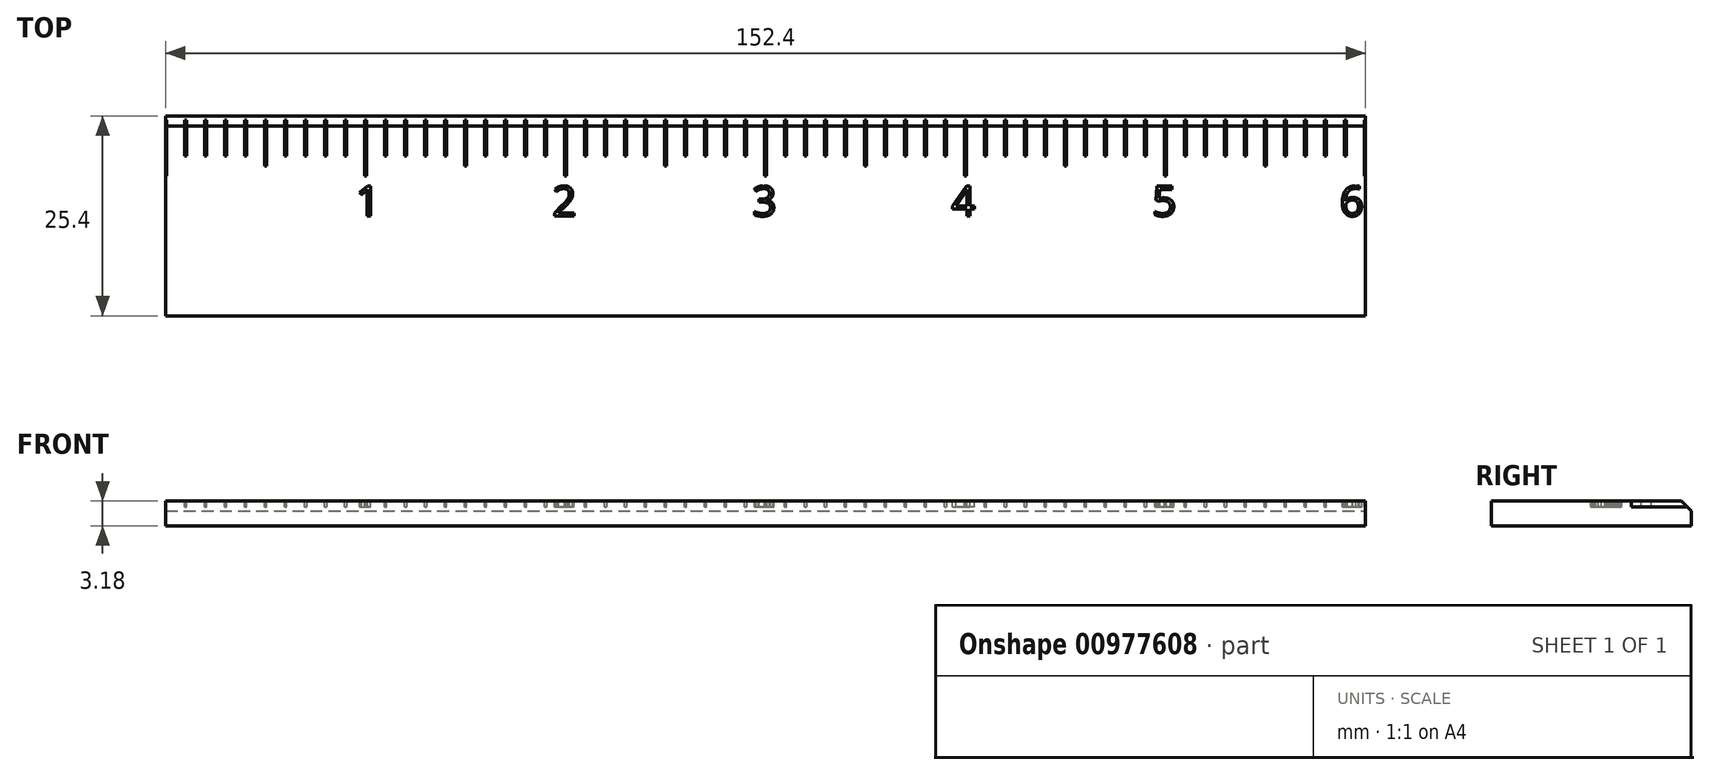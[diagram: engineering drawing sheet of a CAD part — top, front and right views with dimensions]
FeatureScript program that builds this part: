
annotation { "Feature Type Name" : "Feature", "Feature Type Description" : "" }
export const myFeature = defineFeature(function(context is Context, id is Id, definition is map)
    precondition{}
    {
        {
            var Q0;
            Q0=qCreatedBy(makeId("Top.planeOp"),FACE);
            var sketch = newSketch(context, id + "F0", { "sketchPlane" : qUnion([Q0])});
            skLineSegment(sketch, "E0.bottom", {"start": v(76.2, -12.7) * mm, "end": v(-76.2, -12.7) * mm});
            skLineSegment(sketch, "E0.top", {"start": v(76.2, 12.7) * mm, "end": v(-76.2, 12.7) * mm});
            skLineSegment(sketch, "E0.left", {"start": v(76.2, -12.7) * mm, "end": v(76.2, 12.7) * mm});
            skLineSegment(sketch, "E0.right", {"start": v(-76.2, -12.7) * mm, "end": v(-76.2, 12.7) * mm});
            skPoint(sketch, "E0.middle", {"position": v(0, 0) * mm});
            skSolve(sketch);
        }
        {
            var Q0;
            Q0 = qSketchRegion(id + "F0", true);
            extrude(context, id + "F1", {"entities" : qUnion([Q0]), "depth" : 3.17 * mm, "offsetDistance" : 25.4 * mm});
        }
        {
            var Q0;
            Q0=makeQuery(id+"F1.opExtrude","CAP_FACE",FACE,{"disambiguationData":[OSD([sQuery(id+"F0.wireOp",EDGE,"E0.bottom"),sQuery(id+"F0.wireOp",EDGE,"E0.top"),sQuery(id+"F0.wireOp",EDGE,"E0.left"),sQuery(id+"F0.wireOp",EDGE,"E0.right")])],"isStart":false});
            var sketch = newSketch(context, id + "F2", { "sketchPlane" : qUnion([Q0])});
            skLineSegment(sketch, "E1.bottom", {"start": v(-76.33, 12.7) * mm, "end": v(-76.07, 12.7) * mm});
            skLineSegment(sketch, "E1.top", {"start": v(-76.33, 5.08) * mm, "end": v(-76.07, 5.08) * mm});
            skLineSegment(sketch, "E1.left", {"start": v(-76.33, 12.7) * mm, "end": v(-76.33, 5.08) * mm});
            skLineSegment(sketch, "E1.right", {"start": v(-76.07, 12.7) * mm, "end": v(-76.07, 5.08) * mm});
            skLineSegment(sketch, "E2.bottom", {"start": v(-73.79, 12.7) * mm, "end": v(-73.53, 12.7) * mm});
            skLineSegment(sketch, "E2.top", {"start": v(-73.79, 7.62) * mm, "end": v(-73.53, 7.62) * mm});
            skLineSegment(sketch, "E2.left", {"start": v(-73.79, 12.7) * mm, "end": v(-73.79, 7.62) * mm});
            skLineSegment(sketch, "E2.right", {"start": v(-73.53, 12.7) * mm, "end": v(-73.53, 7.62) * mm});
            skLineSegment(sketch, "E3.1.0.0", {"start": v(-71.25, 12.7) * mm, "end": v(-71.25, 7.62) * mm});
            skLineSegment(sketch, "E3.1.0.1", {"start": v(-71, 12.7) * mm, "end": v(-71, 7.62) * mm});
            skLineSegment(sketch, "E3.1.0.2", {"start": v(-71.25, 12.7) * mm, "end": v(-71, 12.7) * mm});
            skLineSegment(sketch, "E3.1.0.3", {"start": v(-71.25, 7.62) * mm, "end": v(-71, 7.62) * mm});
            skLineSegment(sketch, "E3.2.0.0", {"start": v(-68.7, 12.7) * mm, "end": v(-68.7, 7.62) * mm});
            skLineSegment(sketch, "E3.2.0.1", {"start": v(-68.45, 12.7) * mm, "end": v(-68.45, 7.62) * mm});
            skLineSegment(sketch, "E3.2.0.2", {"start": v(-68.7, 12.7) * mm, "end": v(-68.45, 12.7) * mm});
            skLineSegment(sketch, "E3.2.0.3", {"start": v(-68.7, 7.62) * mm, "end": v(-68.45, 7.62) * mm});
            skLineSegment(sketch, "E3.3.0.0", {"start": v(-66.17, 12.7) * mm, "end": v(-66.17, 7.62) * mm});
            skLineSegment(sketch, "E3.3.0.1", {"start": v(-65.91, 12.7) * mm, "end": v(-65.91, 7.62) * mm});
            skLineSegment(sketch, "E3.3.0.2", {"start": v(-66.17, 12.7) * mm, "end": v(-65.91, 12.7) * mm});
            skLineSegment(sketch, "E3.3.0.3", {"start": v(-66.17, 7.62) * mm, "end": v(-65.91, 7.62) * mm});
            skLineSegment(sketch, "E3.direction1", {"start": v(-73.79, 7.62) * mm, "end": v(-71.25, 7.62) * mm, "construction": true});
            skLineSegment(sketch, "E4.bottom", {"start": v(-63.63, 12.7) * mm, "end": v(-63.37, 12.7) * mm});
            skLineSegment(sketch, "E4.top", {"start": v(-63.63, 6.35) * mm, "end": v(-63.37, 6.35) * mm});
            skLineSegment(sketch, "E4.left", {"start": v(-63.63, 12.7) * mm, "end": v(-63.63, 6.35) * mm});
            skLineSegment(sketch, "E4.right", {"start": v(-63.37, 12.7) * mm, "end": v(-63.37, 6.35) * mm});
            skLineSegment(sketch, "E5.bottom", {"start": v(-61.09, 12.7) * mm, "end": v(-60.83, 12.7) * mm});
            skLineSegment(sketch, "E5.top", {"start": v(-61.09, 7.62) * mm, "end": v(-60.83, 7.62) * mm});
            skLineSegment(sketch, "E5.left", {"start": v(-61.09, 12.7) * mm, "end": v(-61.09, 7.62) * mm});
            skLineSegment(sketch, "E5.right", {"start": v(-60.83, 12.7) * mm, "end": v(-60.83, 7.62) * mm});
            skLineSegment(sketch, "E6.1.0.0", {"start": v(-58.3, 12.7) * mm, "end": v(-58.3, 7.62) * mm});
            skLineSegment(sketch, "E6.1.0.1", {"start": v(-58.55, 12.7) * mm, "end": v(-58.55, 7.62) * mm});
            skLineSegment(sketch, "E6.1.0.2", {"start": v(-58.55, 12.7) * mm, "end": v(-58.3, 12.7) * mm});
            skLineSegment(sketch, "E6.1.0.3", {"start": v(-58.55, 7.62) * mm, "end": v(-58.3, 7.62) * mm});
            skLineSegment(sketch, "E6.2.0.0", {"start": v(-55.75, 12.7) * mm, "end": v(-55.75, 7.62) * mm});
            skLineSegment(sketch, "E6.2.0.1", {"start": v(-56, 12.7) * mm, "end": v(-56, 7.62) * mm});
            skLineSegment(sketch, "E6.2.0.2", {"start": v(-56, 12.7) * mm, "end": v(-55.75, 12.7) * mm});
            skLineSegment(sketch, "E6.2.0.3", {"start": v(-56, 7.62) * mm, "end": v(-55.75, 7.62) * mm});
            skLineSegment(sketch, "E6.3.0.0", {"start": v(-53.21, 12.7) * mm, "end": v(-53.21, 7.62) * mm});
            skLineSegment(sketch, "E6.3.0.1", {"start": v(-53.47, 12.7) * mm, "end": v(-53.47, 7.62) * mm});
            skLineSegment(sketch, "E6.3.0.2", {"start": v(-53.47, 12.7) * mm, "end": v(-53.21, 12.7) * mm});
            skLineSegment(sketch, "E6.3.0.3", {"start": v(-53.47, 7.62) * mm, "end": v(-53.21, 7.62) * mm});
            skLineSegment(sketch, "E6.direction1", {"start": v(-61.09, 7.62) * mm, "end": v(-58.55, 7.62) * mm, "construction": true});
            skLineSegment(sketch, "E7.bottom", {"start": v(-50.93, 12.7) * mm, "end": v(-50.67, 12.7) * mm});
            skLineSegment(sketch, "E7.top", {"start": v(-50.93, 5.08) * mm, "end": v(-50.67, 5.08) * mm});
            skLineSegment(sketch, "E7.left", {"start": v(-50.93, 12.7) * mm, "end": v(-50.93, 5.08) * mm});
            skLineSegment(sketch, "E7.right", {"start": v(-50.67, 12.7) * mm, "end": v(-50.67, 5.08) * mm});
            skLineSegment(sketch, "E8.1.0.0", {"start": v(-45.6, 12.7) * mm, "end": v(-45.6, 7.62) * mm});
            skLineSegment(sketch, "E8.1.0.2", {"start": v(-48.39, 12.7) * mm, "end": v(-48.39, 7.62) * mm});
            skLineSegment(sketch, "E8.1.0.3", {"start": v(-33.15, 12.7) * mm, "end": v(-33.15, 7.62) * mm});
            skLineSegment(sketch, "E8.1.0.4", {"start": v(-32.9, 12.7) * mm, "end": v(-32.9, 7.62) * mm});
            skLineSegment(sketch, "E8.1.0.5", {"start": v(-45.85, 12.7) * mm, "end": v(-45.85, 7.62) * mm});
            skLineSegment(sketch, "E8.1.0.6", {"start": v(-35.69, 12.7) * mm, "end": v(-35.69, 7.62) * mm});
            skLineSegment(sketch, "E8.1.0.7", {"start": v(-30.6, 12.7) * mm, "end": v(-30.6, 7.62) * mm});
            skLineSegment(sketch, "E8.1.0.8", {"start": v(-38.23, 12.7) * mm, "end": v(-38.23, 6.35) * mm});
            skLineSegment(sketch, "E8.1.0.9", {"start": v(-43.05, 12.7) * mm, "end": v(-43.05, 7.62) * mm});
            skLineSegment(sketch, "E8.1.0.10", {"start": v(-35.43, 12.7) * mm, "end": v(-35.43, 7.62) * mm});
            skLineSegment(sketch, "E8.1.0.11", {"start": v(-48.13, 12.7) * mm, "end": v(-48.13, 7.62) * mm});
            skLineSegment(sketch, "E8.1.0.12", {"start": v(-40.77, 12.7) * mm, "end": v(-40.77, 7.62) * mm});
            skLineSegment(sketch, "E8.1.0.13", {"start": v(-25.53, 12.7) * mm, "end": v(-25.53, 5.08) * mm});
            skLineSegment(sketch, "E8.1.0.14", {"start": v(-37.97, 12.7) * mm, "end": v(-37.97, 6.35) * mm});
            skLineSegment(sketch, "E8.1.0.15", {"start": v(-43.3, 12.7) * mm, "end": v(-43.3, 7.62) * mm});
            skLineSegment(sketch, "E8.1.0.17", {"start": v(-27.81, 12.7) * mm, "end": v(-27.81, 7.62) * mm});
            skLineSegment(sketch, "E8.1.0.18", {"start": v(-48.39, 7.62) * mm, "end": v(-45.85, 7.62) * mm, "construction": true});
            skLineSegment(sketch, "E8.1.0.19", {"start": v(-30.35, 12.7) * mm, "end": v(-30.35, 7.62) * mm});
            skLineSegment(sketch, "E8.1.0.20", {"start": v(-25.27, 12.7) * mm, "end": v(-25.27, 5.08) * mm});
            skLineSegment(sketch, "E8.1.0.21", {"start": v(-35.69, 7.62) * mm, "end": v(-33.15, 7.62) * mm, "construction": true});
            skLineSegment(sketch, "E8.1.0.22", {"start": v(-40.51, 12.7) * mm, "end": v(-40.51, 7.62) * mm});
            skLineSegment(sketch, "E8.1.0.23", {"start": v(-28.07, 12.7) * mm, "end": v(-28.07, 7.62) * mm});
            skLineSegment(sketch, "E8.1.0.24", {"start": v(-30.6, 7.62) * mm, "end": v(-30.35, 7.62) * mm});
            skLineSegment(sketch, "E8.1.0.25", {"start": v(-40.77, 12.7) * mm, "end": v(-40.51, 12.7) * mm});
            skLineSegment(sketch, "E8.1.0.26", {"start": v(-45.85, 12.7) * mm, "end": v(-45.6, 12.7) * mm});
            skLineSegment(sketch, "E8.1.0.27", {"start": v(-40.77, 7.62) * mm, "end": v(-40.51, 7.62) * mm});
            skLineSegment(sketch, "E8.1.0.28", {"start": v(-33.15, 12.7) * mm, "end": v(-32.9, 12.7) * mm});
            skLineSegment(sketch, "E8.1.0.29", {"start": v(-30.6, 12.7) * mm, "end": v(-30.35, 12.7) * mm});
            skLineSegment(sketch, "E8.1.0.30", {"start": v(-38.23, 12.7) * mm, "end": v(-37.97, 12.7) * mm});
            skLineSegment(sketch, "E8.1.0.33", {"start": v(-35.69, 12.7) * mm, "end": v(-35.43, 12.7) * mm});
            skLineSegment(sketch, "E8.1.0.34", {"start": v(-48.39, 12.7) * mm, "end": v(-48.13, 12.7) * mm});
            skLineSegment(sketch, "E8.1.0.35", {"start": v(-25.53, 5.08) * mm, "end": v(-25.27, 5.08) * mm});
            skLineSegment(sketch, "E8.1.0.36", {"start": v(-25.53, 12.7) * mm, "end": v(-25.27, 12.7) * mm});
            skLineSegment(sketch, "E8.1.0.37", {"start": v(-43.3, 12.7) * mm, "end": v(-43.05, 12.7) * mm});
            skLineSegment(sketch, "E8.1.0.38", {"start": v(-38.23, 6.35) * mm, "end": v(-37.97, 6.35) * mm});
            skLineSegment(sketch, "E8.1.0.39", {"start": v(-43.3, 7.62) * mm, "end": v(-43.05, 7.62) * mm});
            skLineSegment(sketch, "E8.1.0.40", {"start": v(-48.39, 7.62) * mm, "end": v(-48.13, 7.62) * mm});
            skLineSegment(sketch, "E8.1.0.41", {"start": v(-33.15, 7.62) * mm, "end": v(-32.9, 7.62) * mm});
            skLineSegment(sketch, "E8.1.0.42", {"start": v(-35.69, 7.62) * mm, "end": v(-35.43, 7.62) * mm});
            skLineSegment(sketch, "E8.1.0.43", {"start": v(-45.85, 7.62) * mm, "end": v(-45.6, 7.62) * mm});
            skLineSegment(sketch, "E8.1.0.44", {"start": v(-28.07, 7.62) * mm, "end": v(-27.81, 7.62) * mm});
            skLineSegment(sketch, "E8.1.0.45", {"start": v(-28.07, 12.7) * mm, "end": v(-27.81, 12.7) * mm});
            skLineSegment(sketch, "E8.2.0.0", {"start": v(-20.2, 12.7) * mm, "end": v(-20.2, 7.62) * mm});
            skLineSegment(sketch, "E8.2.0.1", {"start": v(-25.27, 12.7) * mm, "end": v(-25.27, 5.08) * mm});
            skLineSegment(sketch, "E8.2.0.2", {"start": v(-22.99, 12.7) * mm, "end": v(-22.99, 7.62) * mm});
            skLineSegment(sketch, "E8.2.0.3", {"start": v(-7.75, 12.7) * mm, "end": v(-7.75, 7.62) * mm});
            skLineSegment(sketch, "E8.2.0.4", {"start": v(-7.5, 12.7) * mm, "end": v(-7.5, 7.62) * mm});
            skLineSegment(sketch, "E8.2.0.5", {"start": v(-20.45, 12.7) * mm, "end": v(-20.45, 7.62) * mm});
            skLineSegment(sketch, "E8.2.0.6", {"start": v(-10.29, 12.7) * mm, "end": v(-10.29, 7.62) * mm});
            skLineSegment(sketch, "E8.2.0.7", {"start": v(-5.2, 12.7) * mm, "end": v(-5.2, 7.62) * mm});
            skLineSegment(sketch, "E8.2.0.8", {"start": v(-12.83, 12.7) * mm, "end": v(-12.83, 6.35) * mm});
            skLineSegment(sketch, "E8.2.0.9", {"start": v(-17.65, 12.7) * mm, "end": v(-17.65, 7.62) * mm});
            skLineSegment(sketch, "E8.2.0.10", {"start": v(-10.03, 12.7) * mm, "end": v(-10.03, 7.62) * mm});
            skLineSegment(sketch, "E8.2.0.11", {"start": v(-22.73, 12.7) * mm, "end": v(-22.73, 7.62) * mm});
            skLineSegment(sketch, "E8.2.0.12", {"start": v(-15.37, 12.7) * mm, "end": v(-15.37, 7.62) * mm});
            skLineSegment(sketch, "E8.2.0.13", {"start": v(-0.13, 12.7) * mm, "end": v(-0.13, 5.08) * mm});
            skLineSegment(sketch, "E8.2.0.14", {"start": v(-12.57, 12.7) * mm, "end": v(-12.57, 6.35) * mm});
            skLineSegment(sketch, "E8.2.0.15", {"start": v(-17.9, 12.7) * mm, "end": v(-17.9, 7.62) * mm});
            skLineSegment(sketch, "E8.2.0.16", {"start": v(-25.53, 12.7) * mm, "end": v(-25.53, 5.08) * mm});
            skLineSegment(sketch, "E8.2.0.17", {"start": v(-2.41, 12.7) * mm, "end": v(-2.41, 7.62) * mm});
            skLineSegment(sketch, "E8.2.0.18", {"start": v(-22.99, 7.62) * mm, "end": v(-20.45, 7.62) * mm, "construction": true});
            skLineSegment(sketch, "E8.2.0.19", {"start": v(-4.95, 12.7) * mm, "end": v(-4.95, 7.62) * mm});
            skLineSegment(sketch, "E8.2.0.20", {"start": v(0.13, 12.7) * mm, "end": v(0.13, 5.08) * mm});
            skLineSegment(sketch, "E8.2.0.21", {"start": v(-10.29, 7.62) * mm, "end": v(-7.75, 7.62) * mm, "construction": true});
            skLineSegment(sketch, "E8.2.0.22", {"start": v(-15.11, 12.7) * mm, "end": v(-15.11, 7.62) * mm});
            skLineSegment(sketch, "E8.2.0.23", {"start": v(-2.67, 12.7) * mm, "end": v(-2.67, 7.62) * mm});
            skLineSegment(sketch, "E8.2.0.24", {"start": v(-5.2, 7.62) * mm, "end": v(-4.95, 7.62) * mm});
            skLineSegment(sketch, "E8.2.0.25", {"start": v(-15.37, 12.7) * mm, "end": v(-15.11, 12.7) * mm});
            skLineSegment(sketch, "E8.2.0.26", {"start": v(-20.45, 12.7) * mm, "end": v(-20.2, 12.7) * mm});
            skLineSegment(sketch, "E8.2.0.27", {"start": v(-15.37, 7.62) * mm, "end": v(-15.11, 7.62) * mm});
            skLineSegment(sketch, "E8.2.0.28", {"start": v(-7.75, 12.7) * mm, "end": v(-7.5, 12.7) * mm});
            skLineSegment(sketch, "E8.2.0.29", {"start": v(-5.2, 12.7) * mm, "end": v(-4.95, 12.7) * mm});
            skLineSegment(sketch, "E8.2.0.30", {"start": v(-12.83, 12.7) * mm, "end": v(-12.57, 12.7) * mm});
            skLineSegment(sketch, "E8.2.0.31", {"start": v(-25.53, 5.08) * mm, "end": v(-25.27, 5.08) * mm});
            skLineSegment(sketch, "E8.2.0.32", {"start": v(-25.53, 12.7) * mm, "end": v(-25.27, 12.7) * mm});
            skLineSegment(sketch, "E8.2.0.33", {"start": v(-10.29, 12.7) * mm, "end": v(-10.03, 12.7) * mm});
            skLineSegment(sketch, "E8.2.0.34", {"start": v(-22.99, 12.7) * mm, "end": v(-22.73, 12.7) * mm});
            skLineSegment(sketch, "E8.2.0.35", {"start": v(-0.13, 5.08) * mm, "end": v(0.13, 5.08) * mm});
            skLineSegment(sketch, "E8.2.0.36", {"start": v(-0.13, 12.7) * mm, "end": v(0.13, 12.7) * mm});
            skLineSegment(sketch, "E8.2.0.37", {"start": v(-17.9, 12.7) * mm, "end": v(-17.65, 12.7) * mm});
            skLineSegment(sketch, "E8.2.0.38", {"start": v(-12.83, 6.35) * mm, "end": v(-12.57, 6.35) * mm});
            skLineSegment(sketch, "E8.2.0.39", {"start": v(-17.9, 7.62) * mm, "end": v(-17.65, 7.62) * mm});
            skLineSegment(sketch, "E8.2.0.40", {"start": v(-22.99, 7.62) * mm, "end": v(-22.73, 7.62) * mm});
            skLineSegment(sketch, "E8.2.0.41", {"start": v(-7.75, 7.62) * mm, "end": v(-7.5, 7.62) * mm});
            skLineSegment(sketch, "E8.2.0.42", {"start": v(-10.29, 7.62) * mm, "end": v(-10.03, 7.62) * mm});
            skLineSegment(sketch, "E8.2.0.43", {"start": v(-20.45, 7.62) * mm, "end": v(-20.2, 7.62) * mm});
            skLineSegment(sketch, "E8.2.0.44", {"start": v(-2.67, 7.62) * mm, "end": v(-2.41, 7.62) * mm});
            skLineSegment(sketch, "E8.2.0.45", {"start": v(-2.67, 12.7) * mm, "end": v(-2.41, 12.7) * mm});
            skLineSegment(sketch, "E8.3.0.0", {"start": v(5.2, 12.7) * mm, "end": v(5.2, 7.62) * mm});
            skLineSegment(sketch, "E8.3.0.1", {"start": v(0.13, 12.7) * mm, "end": v(0.13, 5.08) * mm});
            skLineSegment(sketch, "E8.3.0.2", {"start": v(2.41, 12.7) * mm, "end": v(2.41, 7.62) * mm});
            skLineSegment(sketch, "E8.3.0.3", {"start": v(17.65, 12.7) * mm, "end": v(17.65, 7.62) * mm});
            skLineSegment(sketch, "E8.3.0.4", {"start": v(17.9, 12.7) * mm, "end": v(17.9, 7.62) * mm});
            skLineSegment(sketch, "E8.3.0.5", {"start": v(4.95, 12.7) * mm, "end": v(4.95, 7.62) * mm});
            skLineSegment(sketch, "E8.3.0.6", {"start": v(15.11, 12.7) * mm, "end": v(15.11, 7.62) * mm});
            skLineSegment(sketch, "E8.3.0.7", {"start": v(20.2, 12.7) * mm, "end": v(20.2, 7.62) * mm});
            skLineSegment(sketch, "E8.3.0.8", {"start": v(12.57, 12.7) * mm, "end": v(12.57, 6.35) * mm});
            skLineSegment(sketch, "E8.3.0.9", {"start": v(7.75, 12.7) * mm, "end": v(7.75, 7.62) * mm});
            skLineSegment(sketch, "E8.3.0.10", {"start": v(15.37, 12.7) * mm, "end": v(15.37, 7.62) * mm});
            skLineSegment(sketch, "E8.3.0.11", {"start": v(2.67, 12.7) * mm, "end": v(2.67, 7.62) * mm});
            skLineSegment(sketch, "E8.3.0.12", {"start": v(10.03, 12.7) * mm, "end": v(10.03, 7.62) * mm});
            skLineSegment(sketch, "E8.3.0.13", {"start": v(25.27, 12.7) * mm, "end": v(25.27, 5.08) * mm});
            skLineSegment(sketch, "E8.3.0.14", {"start": v(12.83, 12.7) * mm, "end": v(12.83, 6.35) * mm});
            skLineSegment(sketch, "E8.3.0.15", {"start": v(7.5, 12.7) * mm, "end": v(7.5, 7.62) * mm});
            skLineSegment(sketch, "E8.3.0.16", {"start": v(-0.13, 12.7) * mm, "end": v(-0.13, 5.08) * mm});
            skLineSegment(sketch, "E8.3.0.17", {"start": v(22.99, 12.7) * mm, "end": v(22.99, 7.62) * mm});
            skLineSegment(sketch, "E8.3.0.18", {"start": v(2.41, 7.62) * mm, "end": v(4.95, 7.62) * mm, "construction": true});
            skLineSegment(sketch, "E8.3.0.19", {"start": v(20.45, 12.7) * mm, "end": v(20.45, 7.62) * mm});
            skLineSegment(sketch, "E8.3.0.20", {"start": v(25.53, 12.7) * mm, "end": v(25.53, 5.08) * mm});
            skLineSegment(sketch, "E8.3.0.21", {"start": v(15.11, 7.62) * mm, "end": v(17.65, 7.62) * mm, "construction": true});
            skLineSegment(sketch, "E8.3.0.22", {"start": v(10.29, 12.7) * mm, "end": v(10.29, 7.62) * mm});
            skLineSegment(sketch, "E8.3.0.23", {"start": v(22.73, 12.7) * mm, "end": v(22.73, 7.62) * mm});
            skLineSegment(sketch, "E8.3.0.24", {"start": v(20.2, 7.62) * mm, "end": v(20.45, 7.62) * mm});
            skLineSegment(sketch, "E8.3.0.25", {"start": v(10.03, 12.7) * mm, "end": v(10.29, 12.7) * mm});
            skLineSegment(sketch, "E8.3.0.26", {"start": v(4.95, 12.7) * mm, "end": v(5.2, 12.7) * mm});
            skLineSegment(sketch, "E8.3.0.27", {"start": v(10.03, 7.62) * mm, "end": v(10.29, 7.62) * mm});
            skLineSegment(sketch, "E8.3.0.28", {"start": v(17.65, 12.7) * mm, "end": v(17.9, 12.7) * mm});
            skLineSegment(sketch, "E8.3.0.29", {"start": v(20.2, 12.7) * mm, "end": v(20.45, 12.7) * mm});
            skLineSegment(sketch, "E8.3.0.30", {"start": v(12.57, 12.7) * mm, "end": v(12.83, 12.7) * mm});
            skLineSegment(sketch, "E8.3.0.31", {"start": v(-0.13, 5.08) * mm, "end": v(0.13, 5.08) * mm});
            skLineSegment(sketch, "E8.3.0.32", {"start": v(-0.13, 12.7) * mm, "end": v(0.13, 12.7) * mm});
            skLineSegment(sketch, "E8.3.0.33", {"start": v(15.11, 12.7) * mm, "end": v(15.37, 12.7) * mm});
            skLineSegment(sketch, "E8.3.0.34", {"start": v(2.41, 12.7) * mm, "end": v(2.67, 12.7) * mm});
            skLineSegment(sketch, "E8.3.0.35", {"start": v(25.27, 5.08) * mm, "end": v(25.53, 5.08) * mm});
            skLineSegment(sketch, "E8.3.0.36", {"start": v(25.27, 12.7) * mm, "end": v(25.53, 12.7) * mm});
            skLineSegment(sketch, "E8.3.0.37", {"start": v(7.5, 12.7) * mm, "end": v(7.75, 12.7) * mm});
            skLineSegment(sketch, "E8.3.0.38", {"start": v(12.57, 6.35) * mm, "end": v(12.83, 6.35) * mm});
            skLineSegment(sketch, "E8.3.0.39", {"start": v(7.5, 7.62) * mm, "end": v(7.75, 7.62) * mm});
            skLineSegment(sketch, "E8.3.0.40", {"start": v(2.41, 7.62) * mm, "end": v(2.67, 7.62) * mm});
            skLineSegment(sketch, "E8.3.0.41", {"start": v(17.65, 7.62) * mm, "end": v(17.9, 7.62) * mm});
            skLineSegment(sketch, "E8.3.0.42", {"start": v(15.11, 7.62) * mm, "end": v(15.37, 7.62) * mm});
            skLineSegment(sketch, "E8.3.0.43", {"start": v(4.95, 7.62) * mm, "end": v(5.2, 7.62) * mm});
            skLineSegment(sketch, "E8.3.0.44", {"start": v(22.73, 7.62) * mm, "end": v(22.99, 7.62) * mm});
            skLineSegment(sketch, "E8.3.0.45", {"start": v(22.73, 12.7) * mm, "end": v(22.99, 12.7) * mm});
            skLineSegment(sketch, "E8.4.0.0", {"start": v(30.6, 12.7) * mm, "end": v(30.6, 7.62) * mm});
            skLineSegment(sketch, "E8.4.0.1", {"start": v(25.53, 12.7) * mm, "end": v(25.53, 5.08) * mm});
            skLineSegment(sketch, "E8.4.0.2", {"start": v(27.81, 12.7) * mm, "end": v(27.81, 7.62) * mm});
            skLineSegment(sketch, "E8.4.0.3", {"start": v(43.05, 12.7) * mm, "end": v(43.05, 7.62) * mm});
            skLineSegment(sketch, "E8.4.0.4", {"start": v(43.3, 12.7) * mm, "end": v(43.3, 7.62) * mm});
            skLineSegment(sketch, "E8.4.0.5", {"start": v(30.35, 12.7) * mm, "end": v(30.35, 7.62) * mm});
            skLineSegment(sketch, "E8.4.0.6", {"start": v(40.51, 12.7) * mm, "end": v(40.51, 7.62) * mm});
            skLineSegment(sketch, "E8.4.0.7", {"start": v(45.6, 12.7) * mm, "end": v(45.6, 7.62) * mm});
            skLineSegment(sketch, "E8.4.0.8", {"start": v(37.97, 12.7) * mm, "end": v(37.97, 6.35) * mm});
            skLineSegment(sketch, "E8.4.0.9", {"start": v(33.15, 12.7) * mm, "end": v(33.15, 7.62) * mm});
            skLineSegment(sketch, "E8.4.0.10", {"start": v(40.77, 12.7) * mm, "end": v(40.77, 7.62) * mm});
            skLineSegment(sketch, "E8.4.0.11", {"start": v(28.07, 12.7) * mm, "end": v(28.07, 7.62) * mm});
            skLineSegment(sketch, "E8.4.0.12", {"start": v(35.43, 12.7) * mm, "end": v(35.43, 7.62) * mm});
            skLineSegment(sketch, "E8.4.0.13", {"start": v(50.67, 12.7) * mm, "end": v(50.67, 5.08) * mm});
            skLineSegment(sketch, "E8.4.0.14", {"start": v(38.23, 12.7) * mm, "end": v(38.23, 6.35) * mm});
            skLineSegment(sketch, "E8.4.0.15", {"start": v(32.9, 12.7) * mm, "end": v(32.9, 7.62) * mm});
            skLineSegment(sketch, "E8.4.0.16", {"start": v(25.27, 12.7) * mm, "end": v(25.27, 5.08) * mm});
            skLineSegment(sketch, "E8.4.0.17", {"start": v(48.39, 12.7) * mm, "end": v(48.39, 7.62) * mm});
            skLineSegment(sketch, "E8.4.0.18", {"start": v(27.81, 7.62) * mm, "end": v(30.35, 7.62) * mm, "construction": true});
            skLineSegment(sketch, "E8.4.0.19", {"start": v(45.85, 12.7) * mm, "end": v(45.85, 7.62) * mm});
            skLineSegment(sketch, "E8.4.0.20", {"start": v(50.93, 12.7) * mm, "end": v(50.93, 5.08) * mm});
            skLineSegment(sketch, "E8.4.0.21", {"start": v(40.51, 7.62) * mm, "end": v(43.05, 7.62) * mm, "construction": true});
            skLineSegment(sketch, "E8.4.0.22", {"start": v(35.69, 12.7) * mm, "end": v(35.69, 7.62) * mm});
            skLineSegment(sketch, "E8.4.0.23", {"start": v(48.13, 12.7) * mm, "end": v(48.13, 7.62) * mm});
            skLineSegment(sketch, "E8.4.0.24", {"start": v(45.6, 7.62) * mm, "end": v(45.85, 7.62) * mm});
            skLineSegment(sketch, "E8.4.0.25", {"start": v(35.43, 12.7) * mm, "end": v(35.69, 12.7) * mm});
            skLineSegment(sketch, "E8.4.0.26", {"start": v(30.35, 12.7) * mm, "end": v(30.6, 12.7) * mm});
            skLineSegment(sketch, "E8.4.0.27", {"start": v(35.43, 7.62) * mm, "end": v(35.69, 7.62) * mm});
            skLineSegment(sketch, "E8.4.0.28", {"start": v(43.05, 12.7) * mm, "end": v(43.3, 12.7) * mm});
            skLineSegment(sketch, "E8.4.0.29", {"start": v(45.6, 12.7) * mm, "end": v(45.85, 12.7) * mm});
            skLineSegment(sketch, "E8.4.0.30", {"start": v(37.97, 12.7) * mm, "end": v(38.23, 12.7) * mm});
            skLineSegment(sketch, "E8.4.0.31", {"start": v(25.27, 5.08) * mm, "end": v(25.53, 5.08) * mm});
            skLineSegment(sketch, "E8.4.0.32", {"start": v(25.27, 12.7) * mm, "end": v(25.53, 12.7) * mm});
            skLineSegment(sketch, "E8.4.0.33", {"start": v(40.51, 12.7) * mm, "end": v(40.77, 12.7) * mm});
            skLineSegment(sketch, "E8.4.0.34", {"start": v(27.81, 12.7) * mm, "end": v(28.07, 12.7) * mm});
            skLineSegment(sketch, "E8.4.0.35", {"start": v(50.67, 5.08) * mm, "end": v(50.93, 5.08) * mm});
            skLineSegment(sketch, "E8.4.0.36", {"start": v(50.67, 12.7) * mm, "end": v(50.93, 12.7) * mm});
            skLineSegment(sketch, "E8.4.0.37", {"start": v(32.9, 12.7) * mm, "end": v(33.15, 12.7) * mm});
            skLineSegment(sketch, "E8.4.0.38", {"start": v(37.97, 6.35) * mm, "end": v(38.23, 6.35) * mm});
            skLineSegment(sketch, "E8.4.0.39", {"start": v(32.9, 7.62) * mm, "end": v(33.15, 7.62) * mm});
            skLineSegment(sketch, "E8.4.0.40", {"start": v(27.81, 7.62) * mm, "end": v(28.07, 7.62) * mm});
            skLineSegment(sketch, "E8.4.0.41", {"start": v(43.05, 7.62) * mm, "end": v(43.3, 7.62) * mm});
            skLineSegment(sketch, "E8.4.0.42", {"start": v(40.51, 7.62) * mm, "end": v(40.77, 7.62) * mm});
            skLineSegment(sketch, "E8.4.0.43", {"start": v(30.35, 7.62) * mm, "end": v(30.6, 7.62) * mm});
            skLineSegment(sketch, "E8.4.0.44", {"start": v(48.13, 7.62) * mm, "end": v(48.39, 7.62) * mm});
            skLineSegment(sketch, "E8.4.0.45", {"start": v(48.13, 12.7) * mm, "end": v(48.39, 12.7) * mm});
            skLineSegment(sketch, "E8.5.0.0", {"start": v(56, 12.7) * mm, "end": v(56, 7.62) * mm});
            skLineSegment(sketch, "E8.5.0.1", {"start": v(50.93, 12.7) * mm, "end": v(50.93, 5.08) * mm});
            skLineSegment(sketch, "E8.5.0.2", {"start": v(53.21, 12.7) * mm, "end": v(53.21, 7.62) * mm});
            skLineSegment(sketch, "E8.5.0.3", {"start": v(68.45, 12.7) * mm, "end": v(68.45, 7.62) * mm});
            skLineSegment(sketch, "E8.5.0.4", {"start": v(68.7, 12.7) * mm, "end": v(68.7, 7.62) * mm});
            skLineSegment(sketch, "E8.5.0.5", {"start": v(55.75, 12.7) * mm, "end": v(55.75, 7.62) * mm});
            skLineSegment(sketch, "E8.5.0.6", {"start": v(65.91, 12.7) * mm, "end": v(65.91, 7.62) * mm});
            skLineSegment(sketch, "E8.5.0.7", {"start": v(71, 12.7) * mm, "end": v(71, 7.62) * mm});
            skLineSegment(sketch, "E8.5.0.8", {"start": v(63.37, 12.7) * mm, "end": v(63.37, 6.35) * mm});
            skLineSegment(sketch, "E8.5.0.9", {"start": v(58.55, 12.7) * mm, "end": v(58.55, 7.62) * mm});
            skLineSegment(sketch, "E8.5.0.10", {"start": v(66.17, 12.7) * mm, "end": v(66.17, 7.62) * mm});
            skLineSegment(sketch, "E8.5.0.11", {"start": v(53.47, 12.7) * mm, "end": v(53.47, 7.62) * mm});
            skLineSegment(sketch, "E8.5.0.12", {"start": v(60.83, 12.7) * mm, "end": v(60.83, 7.62) * mm});
            skLineSegment(sketch, "E8.5.0.13", {"start": v(76.07, 12.7) * mm, "end": v(76.07, 5.08) * mm});
            skLineSegment(sketch, "E8.5.0.14", {"start": v(63.63, 12.7) * mm, "end": v(63.63, 6.35) * mm});
            skLineSegment(sketch, "E8.5.0.15", {"start": v(58.3, 12.7) * mm, "end": v(58.3, 7.62) * mm});
            skLineSegment(sketch, "E8.5.0.16", {"start": v(50.67, 12.7) * mm, "end": v(50.67, 5.08) * mm});
            skLineSegment(sketch, "E8.5.0.17", {"start": v(73.79, 12.7) * mm, "end": v(73.79, 7.62) * mm});
            skLineSegment(sketch, "E8.5.0.18", {"start": v(53.21, 7.62) * mm, "end": v(55.75, 7.62) * mm, "construction": true});
            skLineSegment(sketch, "E8.5.0.19", {"start": v(71.25, 12.7) * mm, "end": v(71.25, 7.62) * mm});
            skLineSegment(sketch, "E8.5.0.20", {"start": v(76.33, 12.7) * mm, "end": v(76.33, 5.08) * mm});
            skLineSegment(sketch, "E8.5.0.21", {"start": v(65.91, 7.62) * mm, "end": v(68.45, 7.62) * mm, "construction": true});
            skLineSegment(sketch, "E8.5.0.22", {"start": v(61.09, 12.7) * mm, "end": v(61.09, 7.62) * mm});
            skLineSegment(sketch, "E8.5.0.23", {"start": v(73.53, 12.7) * mm, "end": v(73.53, 7.62) * mm});
            skLineSegment(sketch, "E8.5.0.24", {"start": v(71, 7.62) * mm, "end": v(71.25, 7.62) * mm});
            skLineSegment(sketch, "E8.5.0.25", {"start": v(60.83, 12.7) * mm, "end": v(61.09, 12.7) * mm});
            skLineSegment(sketch, "E8.5.0.26", {"start": v(55.75, 12.7) * mm, "end": v(56, 12.7) * mm});
            skLineSegment(sketch, "E8.5.0.27", {"start": v(60.83, 7.62) * mm, "end": v(61.09, 7.62) * mm});
            skLineSegment(sketch, "E8.5.0.28", {"start": v(68.45, 12.7) * mm, "end": v(68.7, 12.7) * mm});
            skLineSegment(sketch, "E8.5.0.29", {"start": v(71, 12.7) * mm, "end": v(71.25, 12.7) * mm});
            skLineSegment(sketch, "E8.5.0.30", {"start": v(63.37, 12.7) * mm, "end": v(63.63, 12.7) * mm});
            skLineSegment(sketch, "E8.5.0.31", {"start": v(50.67, 5.08) * mm, "end": v(50.93, 5.08) * mm});
            skLineSegment(sketch, "E8.5.0.32", {"start": v(50.67, 12.7) * mm, "end": v(50.93, 12.7) * mm});
            skLineSegment(sketch, "E8.5.0.33", {"start": v(65.91, 12.7) * mm, "end": v(66.17, 12.7) * mm});
            skLineSegment(sketch, "E8.5.0.34", {"start": v(53.21, 12.7) * mm, "end": v(53.47, 12.7) * mm});
            skLineSegment(sketch, "E8.5.0.35", {"start": v(76.07, 5.08) * mm, "end": v(76.33, 5.08) * mm});
            skLineSegment(sketch, "E8.5.0.36", {"start": v(76.07, 12.7) * mm, "end": v(76.33, 12.7) * mm});
            skLineSegment(sketch, "E8.5.0.37", {"start": v(58.3, 12.7) * mm, "end": v(58.55, 12.7) * mm});
            skLineSegment(sketch, "E8.5.0.38", {"start": v(63.37, 6.35) * mm, "end": v(63.63, 6.35) * mm});
            skLineSegment(sketch, "E8.5.0.39", {"start": v(58.3, 7.62) * mm, "end": v(58.55, 7.62) * mm});
            skLineSegment(sketch, "E8.5.0.40", {"start": v(53.21, 7.62) * mm, "end": v(53.47, 7.62) * mm});
            skLineSegment(sketch, "E8.5.0.41", {"start": v(68.45, 7.62) * mm, "end": v(68.7, 7.62) * mm});
            skLineSegment(sketch, "E8.5.0.42", {"start": v(65.91, 7.62) * mm, "end": v(66.17, 7.62) * mm});
            skLineSegment(sketch, "E8.5.0.43", {"start": v(55.75, 7.62) * mm, "end": v(56, 7.62) * mm});
            skLineSegment(sketch, "E8.5.0.44", {"start": v(73.53, 7.62) * mm, "end": v(73.79, 7.62) * mm});
            skLineSegment(sketch, "E8.5.0.45", {"start": v(73.53, 12.7) * mm, "end": v(73.79, 12.7) * mm});
            skLineSegment(sketch, "E8.direction1", {"start": v(-76.33, 5.08) * mm, "end": v(-50.93, 5.08) * mm, "construction": true});
            skSolve(sketch);
        }
        {
            var Q0;
            {var subQ87=sQuery(id+"F2.wireOp",EDGE,"E1.right");Q0=makeQuery(id+"F2.imprint","IMPRINT",FACE,{"disambiguationData":[TD([[makeQuery(id+"F2.imprint","IMPRINT",EDGE,{"derivedFrom":subQ87}),1.0]])]});}
            var sketch = newSketch(context, id + "F3", { "sketchPlane" : qUnion([Q0])});
            skText(sketch, "E9", { "text": "1", "fontName": "OpenSans-Regular.ttf"});
            skText(sketch, "E10", { "text": "2", "fontName": "OpenSans-Regular.ttf"});
            skText(sketch, "E11", { "text": "3", "fontName": "OpenSans-Regular.ttf"});
            skText(sketch, "E12", { "text": "4", "fontName": "OpenSans-Regular.ttf"});
            skText(sketch, "E13", { "text": "5", "fontName": "OpenSans-Regular.ttf"});
            skText(sketch, "E14", { "text": "6", "fontName": "OpenSans-Regular.ttf"});
            const initialGuessF3  = {"E9": [-0.05202, 0, 1, 0, 0.00381], "E10": [-0.02707, 0, 1, 0, 0.00381], "E11": [-0.00166, 0, 1, 0, 0.00381], "E12": [0.02364, 0, 1, 0, 0.00381], "E13": [0.04914, 0, 1, 0, 0.00381], "E14": [0.07296, 0, 1, 0, 0.00381]};
            skSetInitialGuess(sketch, initialGuessF3);
            skSolve(sketch);
        }
        {
            var Q0;
            Q0 = qSketchRegion(id + "F2", true);
            var Q1;
            Q1 = qSketchRegion(id + "F3", true);
            extrude(context, id + "F4", {"entities" : qUnion([Q0, Q1]), "operationType" : NewBodyOperationType.REMOVE, "oppositeDirection" : true, "depth" : 0.76 * mm, "offsetDistance" : 25.4 * mm});
        }
        {
            var Q0;
            {var subQ0=sQuery(id+"F0.wireOp",EDGE,"E0.top");Q0=makeQuery(id+"F4.boolean.opBoolean","SPLIT",EDGE,{"disambiguationData":[TD([makeQuery(id+"F4.opExtrude","SWEPT_FACE",FACE,{"disambiguationData":[OSD([sQuery(id+"F2.wireOp",EDGE,"E8.5.0.13")])]})])],"derivedFrom":makeQuery(id+"F1.opExtrude","CAP_EDGE",EDGE,{"disambiguationData":[OSD([subQ0])],"isStart":false})});}
            chamfer(context, id + "F5", {"entities" : qUnion([Q0]), "width" : 1.27 * mm, "tangentPropagation" : true});
        }
    });
